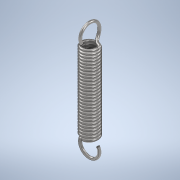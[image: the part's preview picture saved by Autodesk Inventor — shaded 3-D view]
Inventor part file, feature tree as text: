
AUTODESK INVENTOR PART (.ipt)
format: ipt  version: 2020.1 (Build 241239000, 239)  size: 658,432 bytes
history: native  units: mm
features: sketch x10, other x4, plane x2, sweep x2, helix x1
ambient origin geometry x8: Origin, YZ Plane, XZ Plane, XY Plane, X Axis, Y Axis, Z Axis, Center Point
bodies: Solid1 (feature_tree)
feature tree (19):
  helix  "Coil1"  [1 undecoded]
  plane  "Work Plane5"
  sketch  "Sketch15"  dims[d3=10.0mm d4=14.3mm d5=272.5mm d6=0.0mm d7=90.0deg d8=90.0deg d9=6.981317mm d10=0.0mm d35=0.0mm]
  sweep  "Sweep5"
  plane  "Work Plane6"
  sketch  "Sketch17"  dims[d37=0.0mm d38=0.0mm]
  sketch  "Sketch18"  dims[d39=0.0mm]
  sweep  "Sweep6"
  sketch  "Sketch20"  dims[d41=0.0mm d42=0.0mm]
  sketch  "Sketch21"  dims[d45=3.5mm d46=3.5mm d47=10.995574mm d48=10.995574mm]
  sketch  "Sketch1"  dims[d1=0.5mm d2=1.565mm]
  other  "Work Axis2"
  sketch  "3D Sketch8"
  other  "3D Intersection3"
  sketch  "Sketch16"  dims[d36=1.75mm]
  other  "Work Axis3"
  sketch  "3D Sketch9"
  other  "3D Intersection4"
  sketch  "Sketch19"  dims[d40=1.75mm]
note: 1 required parameter value undecoded (feature->parameter linkage not recoverable at this tier; creation-order binding heuristic only, values carry confidence <= 0.55)
